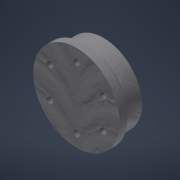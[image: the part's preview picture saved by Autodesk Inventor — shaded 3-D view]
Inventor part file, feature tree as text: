
AUTODESK INVENTOR PART (.ipt)
format: ipt  version: 2022 (Build 260153000, 153)  size: 168,448 bytes
history: native  units: mm
features: reference x7, sketch x6, extrude x4, chamfer x2, projected_geometry x2, other x2, plane x1, hole x1, pattern_circular x1
ambient origin geometry x8: Origin, YZ Plane, XZ Plane, XY Plane, X Axis, Y Axis, Z Axis, Center Point
bodies: Solid1 (feature_tree)
feature tree (26):
  sketch  "Sketch1"  dims[d2=10.0mm d3=0.0mm d4=45.0mm]
  extrude  "Extrusion1"  Depth=10.0mm
  extrude  "Extrusion2"  Depth=3.0mm TaperAngle=0.0deg
  plane  "Work Plane1"
  extrude  "Extrusion3"  Depth=32.0mm
  sketch  "Sketch5"  dims[d16=3.242mm d17=10.0mm d18=4.0mm d19=2.0mm d20=90.0deg d21=11.0mm d22=20.594885mm d23=60.0mm d24=360.0deg]
  chamfer  "Chamfer2"  Distance=60.0mm Angle=360.0deg
  hole  "Hole1"  [1 undecoded]
  pattern_circular  "Circular Pattern1"  [2 undecoded]
  extrude  "Extrusion4"  [1 undecoded]
  chamfer  "Chamfer3"  [1 undecoded]
  sketch  "Sketch2"  dims[d5=4.0mm d6=0.0mm d7=3.0mm d8=0.0mm]
  reference  "Reference1"
  sketch  "Sketch3"  dims[d12=2.0mm d13=2.0mm d14=45.0deg d15=32.0mm]
  reference  "Reference2"
  reference  "Reference3"
  reference  "Reference4"
  reference  "Reference5"
  projected_geometry  "Projected Loop1"
  projected_geometry  "Projected Loop2"
  sketch  "Sketch6"  dims[d26=40.0mm d27=10.0mm d28=0.0mm]
  sketch  "Sketch7"  dims[d29=2.0mm d30=2.0mm d31=45.0deg]
  reference  "Reference6"
  reference  "Reference7"
  other  "SistemaElevacionV2.iam"
  other  "Tornillo de elevación:1"
note: 5 required parameter values undecoded (feature->parameter linkage not recoverable at this tier; creation-order binding heuristic only, values carry confidence <= 0.55)
